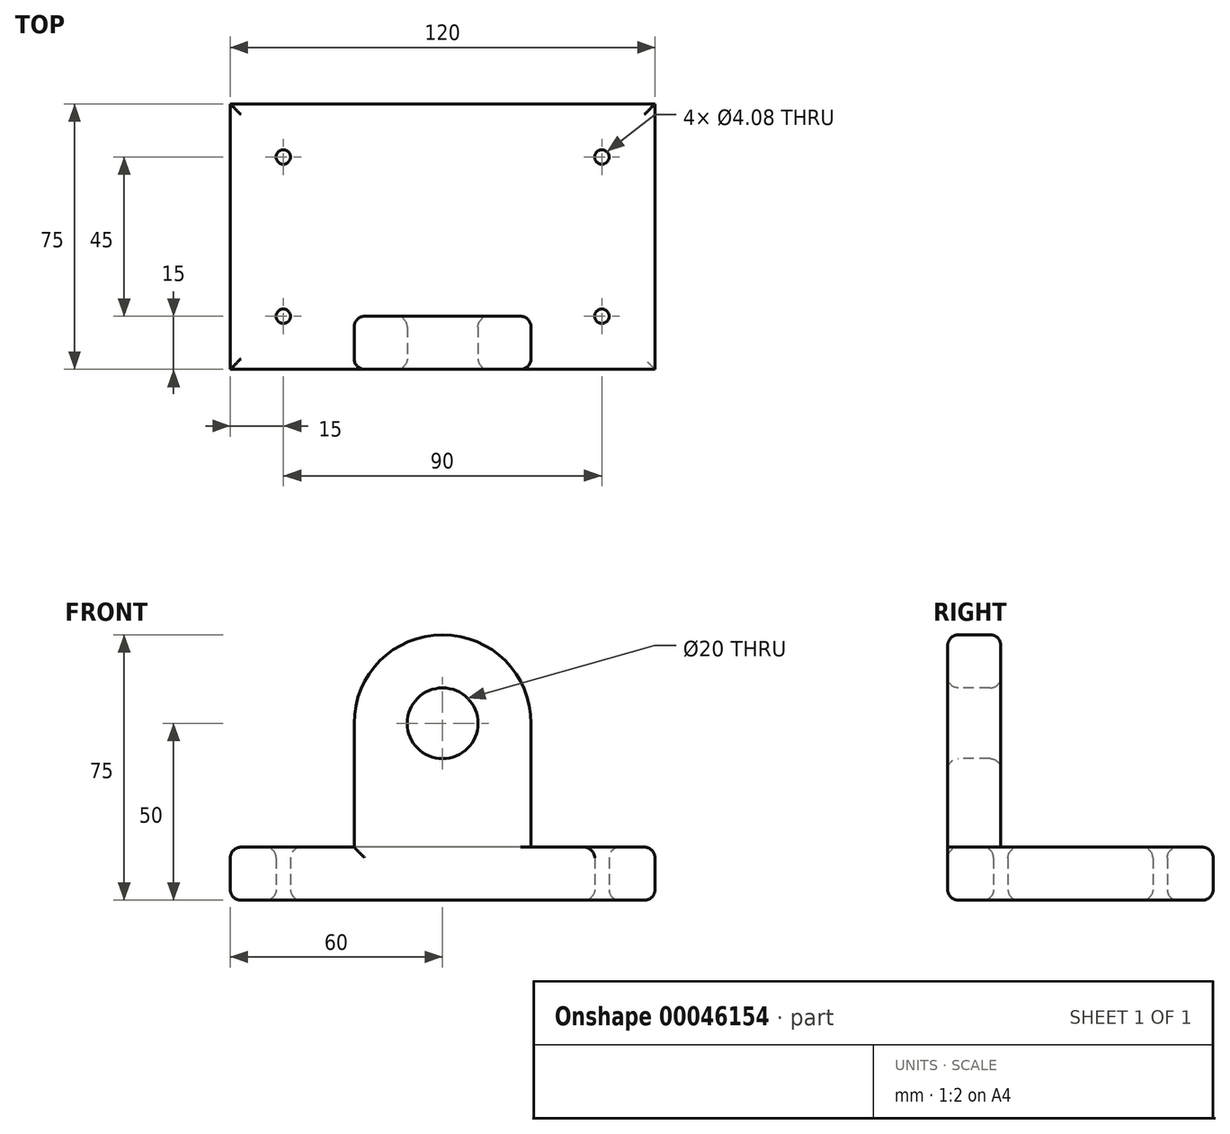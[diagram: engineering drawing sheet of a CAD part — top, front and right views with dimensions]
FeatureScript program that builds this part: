
annotation { "Feature Type Name" : "Feature", "Feature Type Description" : "" }
export const myFeature = defineFeature(function(context is Context, id is Id, definition is map)
    precondition{}
    {
        {
            var Q0;
            Q0=qCreatedBy(makeId("Top.planeOp"),FACE);
            var sketch = newSketch(context, id + "F0", { "sketchPlane" : qUnion([Q0])});
            skLineSegment(sketch, "E0.rect.bottom", {"start": v(60, -37.5) * mm, "end": v(-60, -37.5) * mm});
            skLineSegment(sketch, "E0.rect.top", {"start": v(60, 37.5) * mm, "end": v(-60, 37.5) * mm});
            skLineSegment(sketch, "E0.rect.left", {"start": v(60, -37.5) * mm, "end": v(60, 37.5) * mm});
            skLineSegment(sketch, "E0.rect.right", {"start": v(-60, -37.5) * mm, "end": v(-60, 37.5) * mm});
            skPoint(sketch, "E0.rect.middle", {"position": v(0, 0) * mm});
            skSolve(sketch);
        }
        {
            var Q0;
            Q0=qSketchRegion(id+"F0",true);
            extrude(context, id + "F1", {"entities" : qUnion([Q0]), "depth" : 15 * mm});
        }
        {
            var Q0;
            Q0=makeQuery(id+"F1.opExtrude","SWEPT_FACE",FACE,{"disambiguationData":[OSD([sQuery(id+"F0.wireOp",EDGE,"E0.rect.bottom")])]});
            var sketch = newSketch(context, id + "F2", { "sketchPlane" : qUnion([Q0])});
            skLineSegment(sketch, "E1", {"start": v(0, 0) * mm, "end": v(0, 50) * mm, "construction": true});
            skCircle(sketch, "E2", {"center": v(0, 50) * mm, "radius": 25 * mm});
            skLineSegment(sketch, "E3", {"start": v(-25, 50) * mm, "end": v(-25, 0) * mm});
            skLineSegment(sketch, "E4", {"start": v(25, 50) * mm, "end": v(25, 0) * mm});
            skLineSegment(sketch, "E5", {"start": v(25, 0) * mm, "end": v(-25, 0) * mm});
            skCircle(sketch, "E6", {"center": v(0, 50) * mm, "radius": 10 * mm});
            skSolve(sketch);
        }
        {
            var Q0;
            {var subQ0=sQuery(id+"F2.wireOp",EDGE,"E2");var subQ2=makeQuery(id+"F2.imprint","INTERSECT",VERTEX,{"derivedFrom":[subQ0,sQuery(id+"F2.wireOp",EDGE,"E3")]});Q0=makeQuery(id+"F2.imprint","IMPRINT",FACE,{"disambiguationData":[TD([[makeQuery(id+"F2.imprint","IMPRINT",EDGE,{"disambiguationData":[TD([[subQ2,1.0]])],"derivedFrom":subQ0}),1.0]])]});}
            var Q1;
            {var subQ3=sQuery(id+"F2.wireOp",EDGE,"E3");var subQ5=sQuery(id+"F2.wireOp",EDGE,"E2");var subQ7=makeQuery(id+"F2.imprint","INTERSECT",VERTEX,{"derivedFrom":[subQ5,subQ3]});Q1=makeQuery(id+"F2.imprint","IMPRINT",FACE,{"disambiguationData":[TD([[makeQuery(id+"F2.imprint","IMPRINT",EDGE,{"disambiguationData":[TD([[subQ7,-1.0]])],"derivedFrom":subQ5}),-1.0]])]});}
            extrude(context, id + "F3", {"entities" : qUnion([Q0, Q1]), "operationType" : NewBodyOperationType.ADD, "oppositeDirection" : true, "depth" : 15 * mm});
        }
        {
            var Q0;
            Q0=qCreatedBy(makeId("Top.planeOp"),FACE);
            var sketch = newSketch(context, id + "F4", { "sketchPlane" : qUnion([Q0])});
            skLineSegment(sketch, "E7.rect.bottom", {"start": v(45, -22.5) * mm, "end": v(-45, -22.5) * mm, "construction": true});
            skLineSegment(sketch, "E7.rect.top", {"start": v(45, 22.5) * mm, "end": v(-45, 22.5) * mm, "construction": true});
            skLineSegment(sketch, "E7.rect.left", {"start": v(45, -22.5) * mm, "end": v(45, 22.5) * mm, "construction": true});
            skLineSegment(sketch, "E7.rect.right", {"start": v(-45, -22.5) * mm, "end": v(-45, 22.5) * mm, "construction": true});
            skPoint(sketch, "E7.rect.middle", {"position": v(0, 0) * mm});
            skCircle(sketch, "E8", {"center": v(-45, 22.5) * mm, "radius": 2.04 * mm});
            skCircle(sketch, "E9", {"center": v(45, 22.5) * mm, "radius": 2.04 * mm});
            skCircle(sketch, "E10", {"center": v(45, -22.5) * mm, "radius": 2.04 * mm});
            skCircle(sketch, "E11", {"center": v(-45, -22.5) * mm, "radius": 2.04 * mm});
            skSolve(sketch);
        }
        {
            var Q0;
            Q0=makeQuery(id+"F4.imprint","IMPRINT",FACE,{"disambiguationData":[TD([[makeQuery(id+"F4.imprint","IMPRINT",EDGE,{"derivedFrom":sQuery(id+"F4.wireOp",EDGE,"E9")}),1.0]])]});
            var Q1;
            Q1=makeQuery(id+"F4.imprint","IMPRINT",FACE,{"disambiguationData":[TD([[makeQuery(id+"F4.imprint","IMPRINT",EDGE,{"derivedFrom":sQuery(id+"F4.wireOp",EDGE,"E8")}),1.0]])]});
            var Q2;
            Q2=makeQuery(id+"F4.imprint","IMPRINT",FACE,{"disambiguationData":[TD([[makeQuery(id+"F4.imprint","IMPRINT",EDGE,{"derivedFrom":sQuery(id+"F4.wireOp",EDGE,"E11")}),1.0]])]});
            var Q3;
            Q3=makeQuery(id+"F4.imprint","IMPRINT",FACE,{"disambiguationData":[TD([[makeQuery(id+"F4.imprint","IMPRINT",EDGE,{"derivedFrom":sQuery(id+"F4.wireOp",EDGE,"E10")}),1.0]])]});
            var Q4;
            Q4=sQuery(id+"F4.wireOp",EDGE,"E8");
            extrude(context, id + "F5", {"entities" : qUnion([Q0, Q1, Q2, Q3]), "operationType" : NewBodyOperationType.REMOVE, "surfaceEntities" : qUnion([Q4]), "endBound" : BoundingType.THROUGH_ALL, "depth" : 25 * mm});
        }
        {
            var Q0;
            Q0=makeQuery(id+"F3.opExtrude","CAP_EDGE",EDGE,{"disambiguationData":[OSD([sQuery(id+"F2.wireOp",EDGE,"E2")])],"isStart":true});
            var Q1;
            Q1=makeQuery(id+"F3.opExtrude","CAP_EDGE",EDGE,{"disambiguationData":[OSD([sQuery(id+"F2.wireOp",EDGE,"E2")])],"isStart":false});
            var Q2;
            Q2=makeQuery(id+"F1.opExtrude","CAP_EDGE",EDGE,{"disambiguationData":[OSD([sQuery(id+"F0.wireOp",EDGE,"E0.rect.left")])],"isStart":false});
            var Q3;
            Q3=makeQuery(id+"F1.opExtrude","CAP_EDGE",EDGE,{"disambiguationData":[OSD([sQuery(id+"F0.wireOp",EDGE,"E0.rect.right")])],"isStart":false});
            var Q4;
            Q4=makeQuery(id+"F1.opExtrude","CAP_EDGE",EDGE,{"disambiguationData":[OSD([sQuery(id+"F0.wireOp",EDGE,"E0.rect.top")])],"isStart":false});
            var Q5;
            {var subQ0=sQuery(id+"F0.wireOp",EDGE,"E0.rect.bottom");var subQ2=sQuery(id+"F0.wireOp",EDGE,"E0.rect.right");Q5=makeQuery(id+"F3.boolean.opBoolean","SPLIT",EDGE,{"disambiguationData":[TD([makeQuery(id+"F1.opExtrude","SWEPT_FACE",FACE,{"disambiguationData":[OSD([subQ2])]})])],"derivedFrom":makeQuery(id+"F1.opExtrude","CAP_EDGE",EDGE,{"disambiguationData":[OSD([subQ0])],"isStart":false})});}
            var Q6;
            Q6=makeQuery(id+"F5.boolean.opBoolean","INTERSECT",EDGE,{"derivedFrom":[makeQuery(id+"F1.opExtrude","CAP_FACE",FACE,{"disambiguationData":[OSD([sQuery(id+"F0.wireOp",EDGE,"E0.rect.bottom"),sQuery(id+"F0.wireOp",EDGE,"E0.rect.top"),sQuery(id+"F0.wireOp",EDGE,"E0.rect.left"),sQuery(id+"F0.wireOp",EDGE,"E0.rect.right")])],"isStart":false}),makeQuery(id+"F5.opExtrude","SWEPT_FACE",FACE,{"disambiguationData":[OSD([sQuery(id+"F4.wireOp",EDGE,"E11")])]})]});
            var Q7;
            Q7=makeQuery(id+"F5.boolean.opBoolean","INTERSECT",EDGE,{"derivedFrom":[makeQuery(id+"F1.opExtrude","CAP_FACE",FACE,{"disambiguationData":[OSD([sQuery(id+"F0.wireOp",EDGE,"E0.rect.bottom"),sQuery(id+"F0.wireOp",EDGE,"E0.rect.top"),sQuery(id+"F0.wireOp",EDGE,"E0.rect.left"),sQuery(id+"F0.wireOp",EDGE,"E0.rect.right")])],"isStart":false}),makeQuery(id+"F5.opExtrude","SWEPT_FACE",FACE,{"disambiguationData":[OSD([sQuery(id+"F4.wireOp",EDGE,"E8")])]})]});
            var Q8;
            Q8=makeQuery(id+"F5.boolean.opBoolean","INTERSECT",EDGE,{"derivedFrom":[makeQuery(id+"F1.opExtrude","CAP_FACE",FACE,{"disambiguationData":[OSD([sQuery(id+"F0.wireOp",EDGE,"E0.rect.bottom"),sQuery(id+"F0.wireOp",EDGE,"E0.rect.top"),sQuery(id+"F0.wireOp",EDGE,"E0.rect.left"),sQuery(id+"F0.wireOp",EDGE,"E0.rect.right")])],"isStart":false}),makeQuery(id+"F5.opExtrude","SWEPT_FACE",FACE,{"disambiguationData":[OSD([sQuery(id+"F4.wireOp",EDGE,"E9")])]})]});
            var Q9;
            Q9=makeQuery(id+"F5.boolean.opBoolean","INTERSECT",EDGE,{"derivedFrom":[makeQuery(id+"F1.opExtrude","CAP_FACE",FACE,{"disambiguationData":[OSD([sQuery(id+"F0.wireOp",EDGE,"E0.rect.bottom"),sQuery(id+"F0.wireOp",EDGE,"E0.rect.top"),sQuery(id+"F0.wireOp",EDGE,"E0.rect.left"),sQuery(id+"F0.wireOp",EDGE,"E0.rect.right")])],"isStart":false}),makeQuery(id+"F5.opExtrude","SWEPT_FACE",FACE,{"disambiguationData":[OSD([sQuery(id+"F4.wireOp",EDGE,"E10")])]})]});
            var Q10;
            Q10=makeQuery(id+"F3.opExtrude","CAP_EDGE",EDGE,{"disambiguationData":[OSD([sQuery(id+"F2.wireOp",EDGE,"E3")])],"isStart":true});
            var Q11;
            Q11=makeQuery(id+"F3.opExtrude","CAP_EDGE",EDGE,{"disambiguationData":[OSD([sQuery(id+"F2.wireOp",EDGE,"E3")])],"isStart":false});
            var Q12;
            Q12=makeQuery(id+"F3.opExtrude","CAP_EDGE",EDGE,{"disambiguationData":[OSD([sQuery(id+"F2.wireOp",EDGE,"E4")])],"isStart":false});
            var Q13;
            Q13=makeQuery(id+"F3.opExtrude","CAP_EDGE",EDGE,{"disambiguationData":[OSD([sQuery(id+"F2.wireOp",EDGE,"E4")])],"isStart":true});
            var Q14;
            Q14=makeQuery(id+"F3.opExtrude","CAP_EDGE",EDGE,{"disambiguationData":[OSD([sQuery(id+"F2.wireOp",EDGE,"E6")])],"isStart":false});
            var Q15;
            Q15=makeQuery(id+"F3.opExtrude","CAP_EDGE",EDGE,{"disambiguationData":[OSD([sQuery(id+"F2.wireOp",EDGE,"E6")])],"isStart":true});
            var Q16;
            Q16=makeQuery(id+"F3.opExtrude","SWEPT_EDGE",EDGE,{"disambiguationData":[OSD([sQuery(id+"F0.wireOp",EDGE,"E0.rect.bottom"),sQuery(id+"F2.wireOp",EDGE,"E3")])]});
            var Q17;
            Q17=makeQuery(id+"F1.opExtrude","CAP_FACE",FACE,{"disambiguationData":[OSD([sQuery(id+"F0.wireOp",EDGE,"E0.rect.bottom"),sQuery(id+"F0.wireOp",EDGE,"E0.rect.top"),sQuery(id+"F0.wireOp",EDGE,"E0.rect.left"),sQuery(id+"F0.wireOp",EDGE,"E0.rect.right")])],"isStart":true});
            fillet(context, id + "F6", {"entities" : qUnion([Q0, Q1, Q2, Q3, Q4, Q5, Q6, Q7, Q8, Q9, Q10, Q11, Q12, Q13, Q14, Q15, Q16, Q17]), "radius" : 3 * mm, "tangentPropagation" : true, "allowEdgeOverflow" : false});
        }
    });
